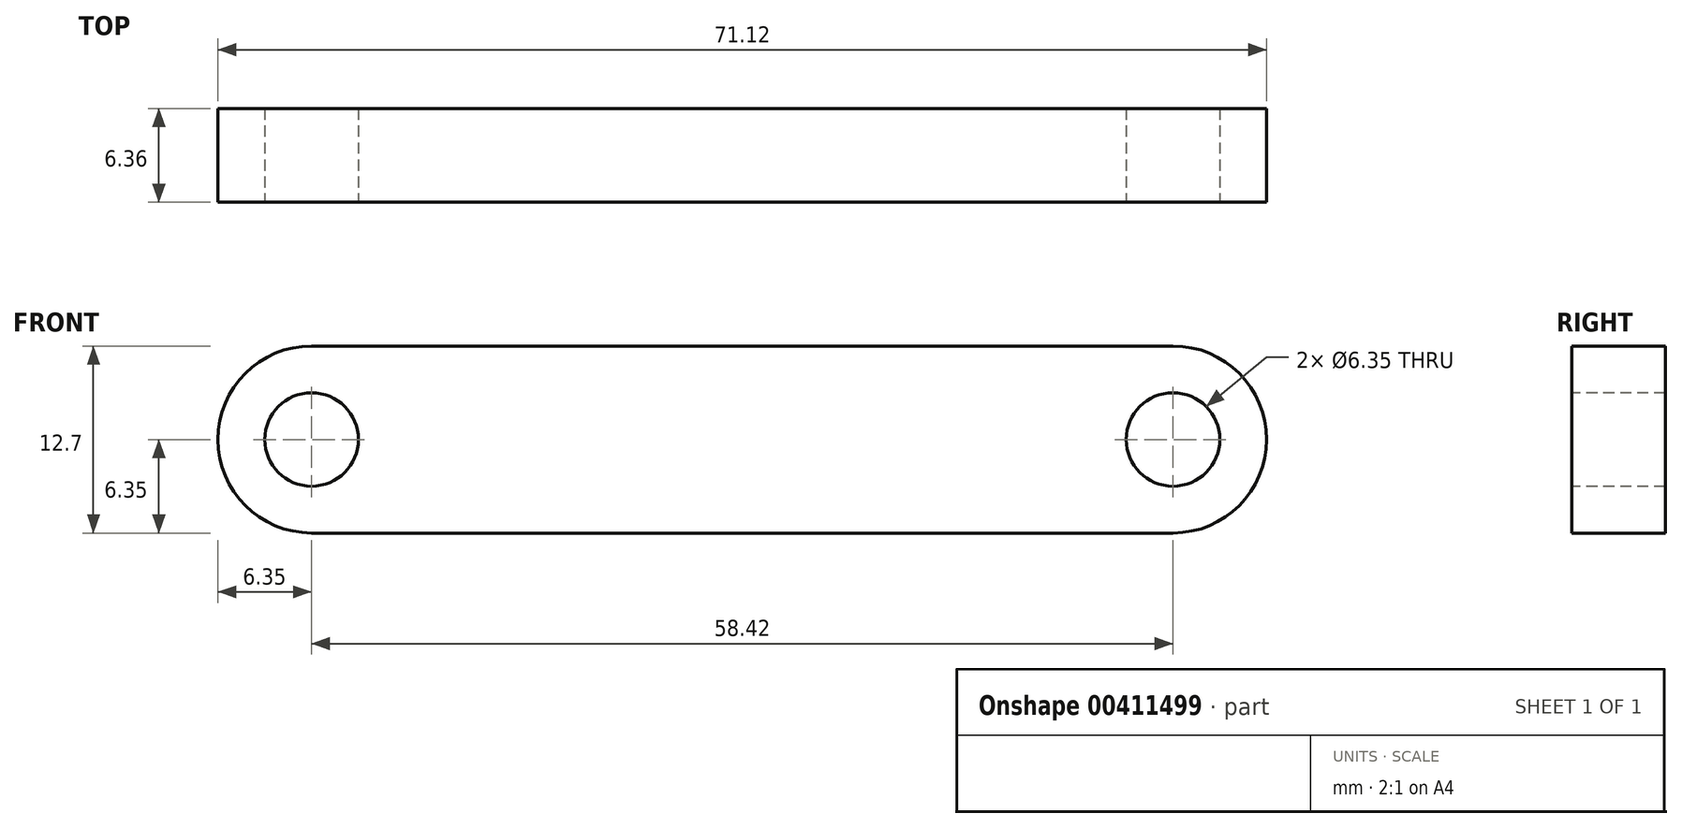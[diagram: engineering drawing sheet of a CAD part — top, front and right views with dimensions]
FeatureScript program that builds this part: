
annotation { "Feature Type Name" : "Feature", "Feature Type Description" : "" }
export const myFeature = defineFeature(function(context is Context, id is Id, definition is map)
    precondition{}
    {
        {
            var Q0;
            Q0=qCreatedBy(makeId("Front.planeOp"),FACE);
            var sketch = newSketch(context, id + "F0", { "sketchPlane" : qUnion([Q0])});
            skLineSegment(sketch, "E0", {"start": v(-35.56, 0) * mm, "end": v(0, 0) * mm, "construction": true});
            skArc(sketch, "E1", {"start": v(-29.21, 6.35) * mm, "mid": v(-33.7, 4.5) * mm, "end": v(-35.56, 0) * mm});
            skLineSegment(sketch, "E2", {"start": v(-29.21, 6.35) * mm, "end": v(0, 6.35) * mm});
            skLineSegment(sketch, "E3", {"start": v(0, 6.35) * mm, "end": v(0, 0) * mm, "construction": true});
            skLineSegment(sketch, "E4.MirrorCS", {"start": v(29.21, 6.35) * mm, "end": v(0, 6.35) * mm});
            skArc(sketch, "E5.MirrorCS", {"start": v(29.21, 6.35) * mm, "mid": v(33.7, 4.5) * mm, "end": v(35.56, 0) * mm});
            skArc(sketch, "E6.MirrorCS", {"start": v(29.21, -6.35) * mm, "mid": v(33.7, -4.5) * mm, "end": v(35.56, 0) * mm});
            skLineSegment(sketch, "E7.MirrorCS", {"start": v(29.21, -6.35) * mm, "end": v(0, -6.35) * mm});
            skLineSegment(sketch, "E8.MirrorCS", {"start": v(-29.21, -6.35) * mm, "end": v(0, -6.35) * mm});
            skArc(sketch, "E9.MirrorCS", {"start": v(-29.21, -6.35) * mm, "mid": v(-33.7, -4.5) * mm, "end": v(-35.56, 0) * mm});
            skSolve(sketch);
        }
        {
            var Q0;
            Q0 = qSketchRegion(id + "F0", true);
            extrude(context, id + "F1", {"entities" : qUnion([Q0]), "endBound" : BoundingType.SYMMETRIC, "depth" : 6.35 * mm});
        }
        {
            var Q0;
            Q0=makeQuery(id+"F1.opExtrude","CAP_FACE",FACE,{"disambiguationData":[OSD([sQuery(id+"F0.wireOp",EDGE,"E1"),sQuery(id+"F0.wireOp",EDGE,"E2"),sQuery(id+"F0.wireOp",EDGE,"E4.MirrorCS"),sQuery(id+"F0.wireOp",EDGE,"E5.MirrorCS"),sQuery(id+"F0.wireOp",EDGE,"E6.MirrorCS"),sQuery(id+"F0.wireOp",EDGE,"E7.MirrorCS"),sQuery(id+"F0.wireOp",EDGE,"E8.MirrorCS"),sQuery(id+"F0.wireOp",EDGE,"E9.MirrorCS")])],"isStart":false});
            var sketch = newSketch(context, id + "F2", { "sketchPlane" : qUnion([Q0])});
            skCircle(sketch, "E10", {"center": v(-29.21, 0) * mm, "radius": 3.18 * mm});
            skLineSegment(sketch, "E11", {"start": v(0, 6.35) * mm, "end": v(0, -6.35) * mm, "construction": true});
            skCircle(sketch, "E12.MirrorC", {"center": v(29.21, 0) * mm, "radius": 3.18 * mm});
            skSolve(sketch);
        }
        {
            var Q0;
            Q0 = qSketchRegion(id + "F2", true);
            extrude(context, id + "F3", {"entities" : qUnion([Q0]), "operationType" : NewBodyOperationType.REMOVE, "endBound" : BoundingType.THROUGH_ALL, "oppositeDirection" : true, "depth" : 25.4 * mm});
        }
    });
